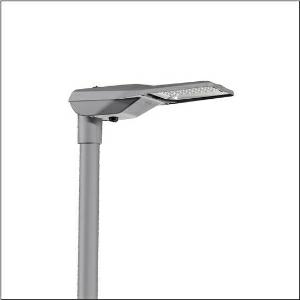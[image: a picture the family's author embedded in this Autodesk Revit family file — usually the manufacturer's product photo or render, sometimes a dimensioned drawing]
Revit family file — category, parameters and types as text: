
# Revit family: streetlight_sl_21_iq_mini___st1_5a_5xe2p31y08hb_ad09
name_source: partatom
category: Lighting Fixtures
units: mm (PartAtom-declared; Revit-internal decimal feet)

## family parameters
Cut with Voids When Loaded = No
Host = Face
Light Source = No
Part Type = Normal
Room Calculation Point = No
Round Connector Dimension = Use Diameter
Shared = No

## types (1)
- --- (1 x LED, 9580 lm, 71 W, 3000K)
    Apparent Load = 71 VA
    CIE Flux Codes = 22 53 95 100 100
    Color Rendering = 70
    Color Temperature = 3000K
    Default Elevation = 1800 mm
    Description = Streetlight SL 21 iQ mini, mast luminaire, primary light control with lens, of PMMA, primary optical cover: cover, of toughened safety glass, transparent, light distribution: ST1.5a, light emission: direct distribution, primary light characteristic: asymmetric, installation type: post-top, side-entry, LED, High Power LED, rated luminous flux: 9.580lm, luminous efficacy: 135lm/W, light colour: 730, colour temperature: 3000K, control gear: iQ-Street Remote, D4i with power reduction, control: pre-setting: logarithmic dimming characteristic, Street-Remote, Auto-Match, Temp-Guard, Lumen-Switch, Night-Set, Smart-Wire, Light-Fading, Desk-Remote (wireless, voltage-free reading and setting of iQ features in the workshop via application-optimized NFC function/RFID function), optimised constant luminous flux control (CLO 2.0), mains connection: 220..240V, AC, 50/60Hz, start of lifetime: 71W, end of service life: 75W, reduction: 30W, luminaire housing, of diecast aluminium, powder-coated, Siteco® metallic grey (DB 702S), corrosivity category C5 mid according to DIN EN ISO 12944, please order mast flange separately, inclination adjustable: 0°, 5°, 10°, 15°, sealing non-destructively replaceable, multi-level sealing system, length: 628mm, width: 235mm, height: 110mm, mast flange for spigot size: 42mm (side-entry): 5XC10008XM4, 60/48mm (side-entry/post-top): 5XC10108XM2, 76/60mm (side-entry/post-top): 5XC10108XM1, mounting height: 4..8m, Smart Interface below and above, protection rating (complete): IP66, insulation class (complete): insulation class II (safety insulation), certification: CE, ENEC, ENEC+, VDE, impact resistance: IK10, permissible operating ambient temperature for outdoor applications: -40..+50°C, standard-compliant lighting for roads and squares, packaging unit: 1 piece

Light Distribution: ST1.5a
    Height = 110 mm
    Lamp = 1 x LED
    Lamp Light Flux = 9580 lm
    Lamp Power = 71 W
    Lamp count = 1
    Length = 625 mm
    Luminous efficacy = 135 lm/W
    Manufacturer = Siteco
    ModVariant = No
    Model = 5XE2P31Y08HB
    Number of Poles = 1
    OnlyDefault = Yes
    Power Factor = 1
    Product Name = Streetlight SL 21 iQ mini | ST1.5a
    Product group = mast luminaire | pylon top
    ProductGroupID = 6100
    Protection Class = Protection class II
    Protection Degree = IP 66
    RLX_Detail_Level = 1
    RLX_Emergency_Light_Flux = 0 lm
    RLX_Emergency_Type = 0
    RLX_Emergency_Type_DB = No
    RlxData = <blob elided: 30169 chars, md5=dbc48990>
    Socket = socket
    Standby Power = 0 W
    System Light Flux = 9580 lm
    System Power = 71 W
    Type Comments = factory setting: luminous flux: 100 % | dim-lin: 254 | 716 mA
    Type Image = l_1003514.jpg
    URL = http://relux.com
    VarID = @adj_111904
    Voltage = 0 V
    Weight = 0.00 kg
    Width = 234 mm

## geometry (parser evidence)
native form markers: Blend x4, Sweep x10
no freeform markers — native parametric forms only
